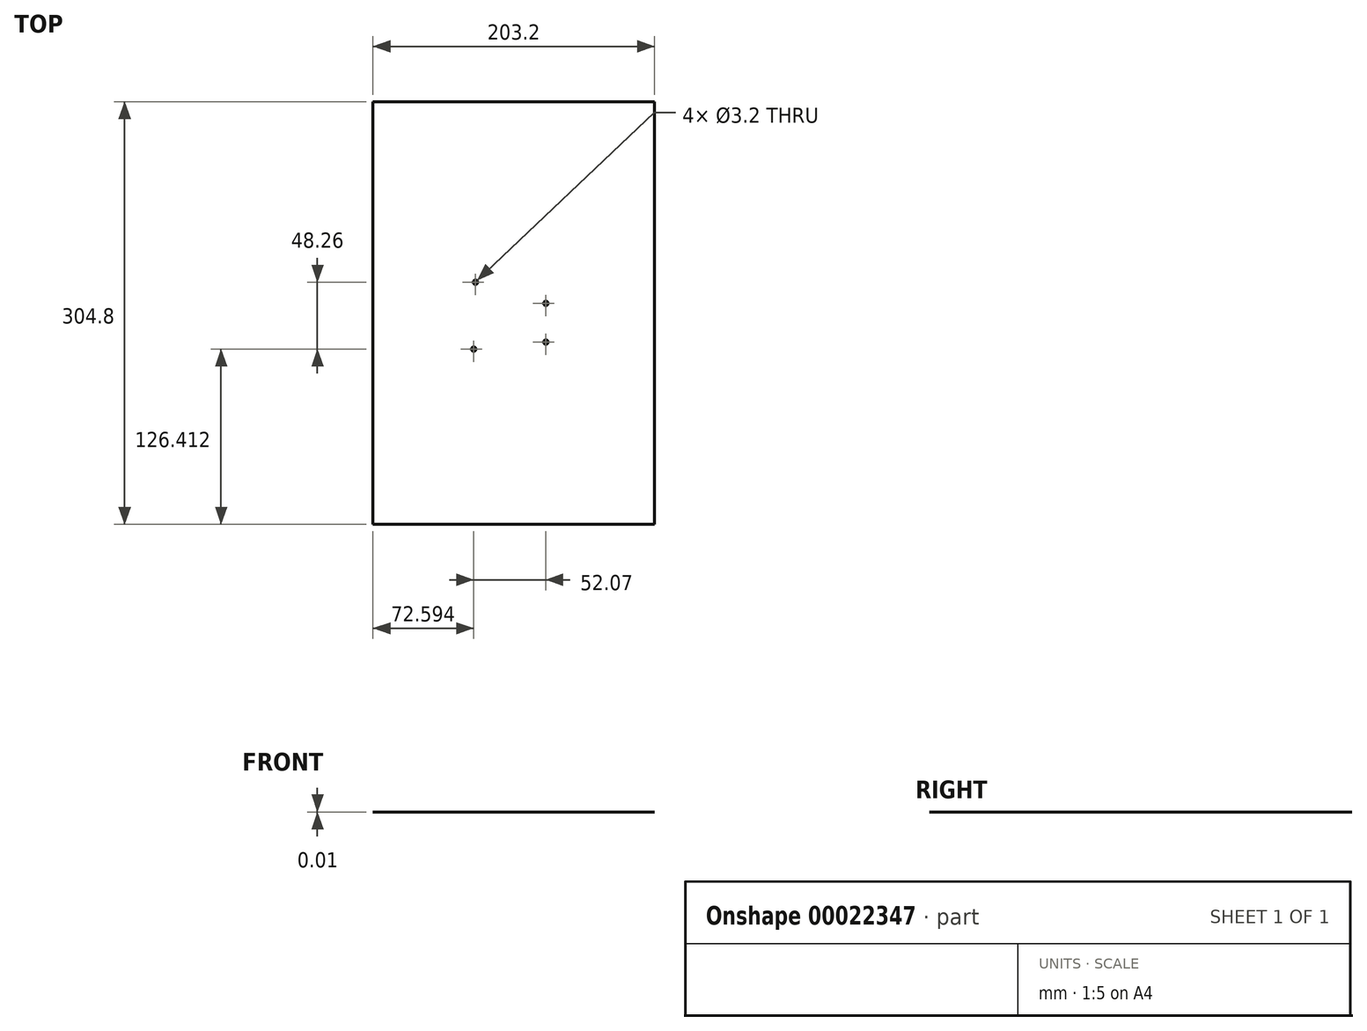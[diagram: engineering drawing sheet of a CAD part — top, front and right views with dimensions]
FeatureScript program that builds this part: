
annotation { "Feature Type Name" : "Feature", "Feature Type Description" : "" }
export const myFeature = defineFeature(function(context is Context, id is Id, definition is map)
    precondition{}
    {
        {
            var Q0;
            Q0=qCreatedBy(makeId("Top.planeOp"),FACE);
            var sketch = newSketch(context, id + "F0", { "sketchPlane" : qUnion([Q0])});
            skLineSegment(sketch, "E0.rect.bottom", {"start": v(101.6, -152.4) * mm, "end": v(-101.6, -152.4) * mm});
            skLineSegment(sketch, "E0.rect.top", {"start": v(101.6, 152.4) * mm, "end": v(-101.6, 152.4) * mm});
            skLineSegment(sketch, "E0.rect.left", {"start": v(101.6, -152.4) * mm, "end": v(101.6, 152.4) * mm});
            skLineSegment(sketch, "E0.rect.right", {"start": v(-101.6, -152.4) * mm, "end": v(-101.6, 152.4) * mm});
            skPoint(sketch, "E0.rect.middle", {"position": v(0, 0) * mm});
            skCircle(sketch, "E1", {"center": v(-27.74, 22.27) * mm, "radius": 1.6 * mm});
            skCircle(sketch, "E2", {"center": v(23.06, 7.03) * mm, "radius": 1.6 * mm});
            skCircle(sketch, "E3", {"center": v(23.06, -20.9) * mm, "radius": 1.6 * mm});
            skCircle(sketch, "E4", {"center": v(-29, -25.99) * mm, "radius": 1.6 * mm});
            skSolve(sketch);
        }
        {
            var Q0;
            Q0=makeQuery(id+"F0.imprint","IMPRINT",FACE,{"disambiguationData":[TD([[makeQuery(id+"F0.imprint","IMPRINT",EDGE,{"derivedFrom":sQuery(id+"F0.wireOp",EDGE,"E0.rect.bottom")}),-1.0]])]});
            extrude(context, id + "F1", {"entities" : qUnion([Q0]), "depth" : 1 / 101.6 * mm});
        }
    });
